# Revit family: Pump_Commercial-Submersible-Zoeller-95_Automatic_Series
name_source: partatom
category: Mechanical Equipment
revit_build: Autodesk Revit 2014 (Build: 20130308_1515(x64)
units: mm (PartAtom-declared; Revit-internal decimal feet)

## types (1)
- M95 - 115V/1Ph/10.5A/1PH
    Amps = 10.5
    Assembly Code = D2090
    Base = Cast Iron
    Cap = Cast Iron
    Cooling = Oil Filled
    Cord Length = 180"
    Cord Type = UL listed, 3-wire, grounded plug
    Default Elevation = 0"
    Description = Automatic Effluent or dewatering submersible pumps for septic tanks, low pressure pipe (LPP) and enhanced flow STEP systems.
    Discharge Diameter = 1 1/2"
    Discharge Height = 5 3/8"
    Discharge Radius = 3/4"
    Gasket = Neoprene
    Hardware = Stainless Steel
    Height = 12 1/8"
    Hertz = 60
    Impeller = Engineered thermoplastic
    Impeller Type = Non-clogging vortex
    Installation Type = Floor Mounted
    Insulation = Class B
    Length = 7 7/8"
    Lower Bearing = Ball Bearing
    Manufacturer = Zoeller
    Material = Cast Iron-Zoeller-Powder Coated Epoxy
    Max Flow @ 5' = 80 GPM
    Max. Water Temp. = 130 °F
    Maximum Head = 312"
    Mechanical Seals = Carbon and Ceramic
    Model = M95
    Motor = 1/2 HP
    Motor Housing = Cast Iron
    Motor Protection = Auto Reset Thermal Overload
    Motor Shaft = ASIS 1215 cold rolled steel
    Motor Type = Submersible
    Off Point = 2 1/2"
    On Point = 9 1/2"
    Operation = Automatic
    Phase = 1
    Price = Prices may vary. Please consult Manufacturer Representative for most up-to-date price list.
    Product Documentation Link = http://cdn.qleapahead.com
    Product Page URL = http://www.zoellerpumps.com
    Pump Housing = Cast Iron
    RPM = 3450
    Solid Handling = 1/2" Spherical Solids
    Type = Permanent Split Capacitor
    URL = http://www.zoellerpumps.com
    Upper Bearing = Sleeve bearing
    Voltage = 115 V
    Warranty Information = 36 Months (Limited)
    Waste Connection = Yes
    Width = 10 3/32"

## geometry (parser evidence)
native form markers: Sweep x3
no freeform markers — native parametric forms only
